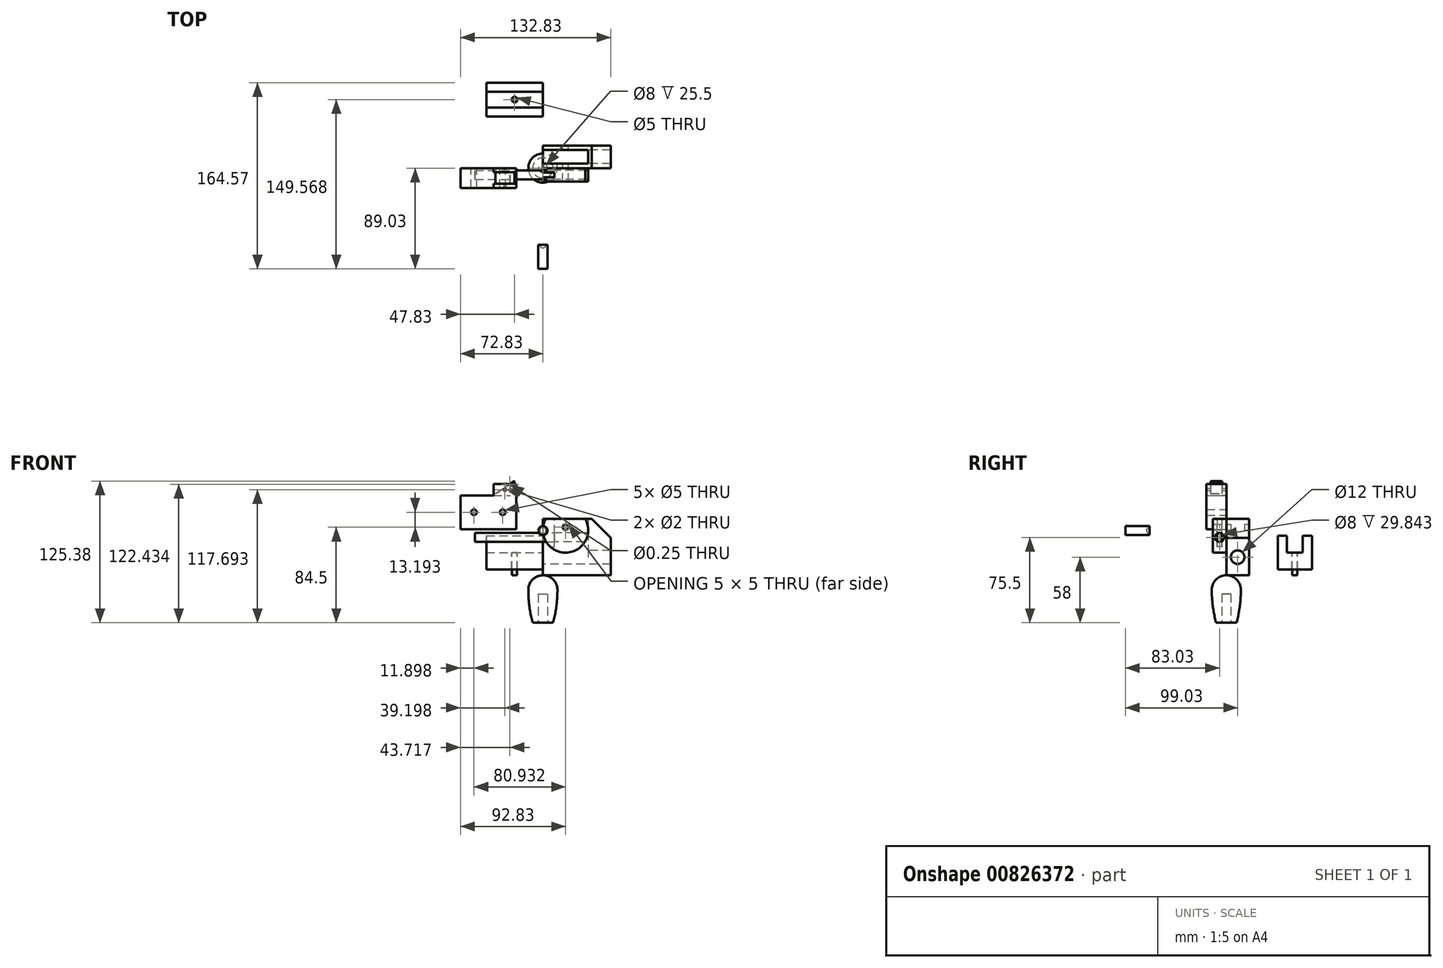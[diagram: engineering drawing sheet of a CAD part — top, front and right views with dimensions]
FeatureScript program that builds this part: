
annotation { "Feature Type Name" : "Feature", "Feature Type Description" : "" }
export const myFeature = defineFeature(function(context is Context, id is Id, definition is map)
    precondition{}
    {
        {
            var Q0;
            Q0=qCreatedBy(makeId("Front.planeOp"),FACE);
            var sketch = newSketch(context, id + "F0", { "sketchPlane" : qUnion([Q0])});
            skLineSegment(sketch, "E0", {"start": v(0, 0) * mm, "end": v(0, 50) * mm});
            skLineSegment(sketch, "E1", {"start": v(0, 50) * mm, "end": v(43, 50) * mm});
            skLineSegment(sketch, "E2", {"start": v(43, 50) * mm, "end": v(60, 33) * mm});
            skLineSegment(sketch, "E3", {"start": v(60, 33) * mm, "end": v(60, 0) * mm});
            skLineSegment(sketch, "E4", {"start": v(60, 0) * mm, "end": v(0, 0) * mm});
            skSolve(sketch);
        }
        {
            var Q0;
            Q0=makeQuery(id+"F0.imprint","IMPRINT",FACE,{"disambiguationData":[TD([[makeQuery(id+"F0.imprint","IMPRINT",EDGE,{"derivedFrom":sQuery(id+"F0.wireOp",EDGE,"E0")}),-1.0]])]});
            extrude(context, id + "F1", {"entities" : qUnion([Q0]), "oppositeDirection" : true, "depth" : 20 * mm, "offsetDistance" : 25 * mm});
        }
        {
            var Q0;
            Q0=makeQuery(id+"F1.opExtrude","SWEPT_FACE",FACE,{"disambiguationData":[OSD([sQuery(id+"F0.wireOp",EDGE,"E0")])]});
            var sketch = newSketch(context, id + "F2", { "sketchPlane" : qUnion([Q0])});
            skLineSegment(sketch, "E5.bottom", {"start": v(-16, 50) * mm, "end": v(-4, 50) * mm});
            skLineSegment(sketch, "E5.top", {"start": v(-16, 16) * mm, "end": v(-4, 16) * mm});
            skLineSegment(sketch, "E5.left", {"start": v(-16, 50) * mm, "end": v(-16, 16) * mm});
            skLineSegment(sketch, "E5.right", {"start": v(-4, 50) * mm, "end": v(-4, 16) * mm});
            skCircle(sketch, "E6", {"center": v(-10, 16) * mm, "radius": 6 * mm});
            skLineSegment(sketch, "E7", {"start": v(-10, 16) * mm, "end": v(-10, 10) * mm});
            skSolve(sketch);
        }
        {
            var Q0;
            Q0 = qSketchRegion(id + "F2", true);
            extrude(context, id + "F3", {"entities" : qUnion([Q0]), "operationType" : NewBodyOperationType.REMOVE, "oppositeDirection" : true, "depth" : 40 * mm, "offsetDistance" : 25 * mm});
        }
        {
            var Q0;
            Q0=makeQuery(id+"F3.boolean.opBoolean","COPY",FACE,{"derivedFrom":makeQuery(id+"F3.opExtrude","CAP_FACE",FACE,{"disambiguationData":[OSD([sQuery(id+"F2.wireOp",EDGE,"E5.bottom"),sQuery(id+"F2.wireOp",EDGE,"E5.left"),sQuery(id+"F2.wireOp",EDGE,"E5.right"),sQuery(id+"F2.wireOp",EDGE,"E6")])],"isStart":false})});
            var sketch = newSketch(context, id + "F4", { "sketchPlane" : qUnion([Q0])});
            skCircle(sketch, "E8", {"center": v(-10, 16) * mm, "radius": 6 * mm});
            skSolve(sketch);
        }
        {
            var Q0;
            {var subQ0=sQuery(id+"F4.wireOp",EDGE,"E8");var subQ1=makeQuery(id+"F4.imprint","INTERSECT",VERTEX,{"derivedFrom":[makeQuery(id+"F3.boolean.opBoolean","COPY",EDGE,{"derivedFrom":makeQuery(id+"F3.opExtrude","CAP_EDGE",EDGE,{"disambiguationData":[OSD([sQuery(id+"F2.wireOp",EDGE,"E5.left")])],"isStart":false})}),subQ0]});Q0=makeQuery(id+"F4.imprint","IMPRINT",FACE,{"disambiguationData":[TD([[makeQuery(id+"F4.imprint","IMPRINT",EDGE,{"disambiguationData":[TD([[subQ1,1.0]])],"derivedFrom":subQ0}),1.0]])]});}
            extrude(context, id + "F5", {"entities" : qUnion([Q0]), "operationType" : NewBodyOperationType.REMOVE, "oppositeDirection" : true, "depth" : 25 * mm, "offsetDistance" : 25 * mm});
        }
        {
            var Q0;
            Q0=qCreatedBy(makeId("Front.planeOp"),FACE);
            var sketch = newSketch(context, id + "F6", { "sketchPlane" : qUnion([Q0])});
            skArc(sketch, "E9", {"start": v(2.68, 50) * mm, "mid": v(20, 20) * mm, "end": v(37.32, 50) * mm});
            skPoint(sketch, "E10", {"position": v(20, 20) * mm});
            skLineSegment(sketch, "E11", {"start": v(2.68, 50) * mm, "end": v(37.32, 50) * mm});
            skSolve(sketch);
        }
        {
            var Q0;
            Q0 = qSketchRegion(id + "F6", true);
            extrude(context, id + "F7", {"entities" : qUnion([Q0]), "depth" : 12 * mm, "offsetDistance" : 25 * mm});
        }
        {
            var Q0;
            Q0=makeQuery(id+"F7.opExtrude","CAP_FACE",FACE,{"disambiguationData":[OSD([sQuery(id+"F6.wireOp",EDGE,"5I9pLb7D-rMst-xJQX-DsKg-gwi81APxeWcW"),sQuery(id+"F6.wireOp",EDGE,"E9")])],"isStart":false});
            var sketch = newSketch(context, id + "F8", { "sketchPlane" : qUnion([Q0])});
            skPoint(sketch, "E12", {"position": v(20, 42.5) * mm});
            skPoint(sketch, "E13", {"position": v(20, 50) * mm});
            skSolve(sketch);
        }
        {
            var Q0;
            Q0=sQuery(id+"F8.wireOp",VERTEX,"E12");
            var Q1;
            Q1=makeQuery(id+"F1.opExtrude","SWEPT_BODY",BODY,{"disambiguationData":[OSD([sQuery(id+"F0.wireOp",EDGE,"E0"),sQuery(id+"F0.wireOp",EDGE,"E1"),sQuery(id+"F0.wireOp",EDGE,"E2"),sQuery(id+"F0.wireOp",EDGE,"E3"),sQuery(id+"F0.wireOp",EDGE,"E4")])]});
            var Q2;
            Q2=makeQuery(id+"F7.opExtrude","SWEPT_BODY",BODY,{"disambiguationData":[OSD([sQuery(id+"F6.wireOp",EDGE,"5I9pLb7D-rMst-xJQX-DsKg-gwi81APxeWcW"),sQuery(id+"F6.wireOp",EDGE,"E9")])]});
            hole(context, id + "F9", {"style" : HoleStyle.SIMPLE, "endStyle" : HoleEndStyle.BLIND, "holeDiameter" : 5 * mm, "majorDiameter" : 5 * mm, "holeDepth" : 50 * mm, "isTappedThrough" : true, "tappedDepth" : 12 * mm, "tapClearance" : 3, "locations" : qUnion([Q0]), "scope" : qUnion([Q1, Q2]), "startStyle" : HoleStartStyle.SKETCH});
        }
        {
            var Q0;
            Q0=makeQuery(id+"F7.opExtrude","SWEPT_FACE",FACE,{"disambiguationData":[OSD([sQuery(id+"F6.wireOp",EDGE,"E11")])]});
            var sketch = newSketch(context, id + "F10", { "sketchPlane" : qUnion([Q0])});
            skLineSegment(sketch, "E14.bottom", {"start": v(0, -3.9) * mm, "end": v(10, -3.9) * mm});
            skLineSegment(sketch, "E14.top", {"start": v(0, -8.1) * mm, "end": v(10, -8.1) * mm});
            skLineSegment(sketch, "E14.left", {"start": v(0, -3.9) * mm, "end": v(0, -8.1) * mm});
            skLineSegment(sketch, "E14.right", {"start": v(10, -3.9) * mm, "end": v(10, -8.1) * mm});
            skSolve(sketch);
        }
        {
            var Q0;
            Q0 = qSketchRegion(id + "F10", true);
            extrude(context, id + "F11", {"entities" : qUnion([Q0]), "operationType" : NewBodyOperationType.REMOVE, "oppositeDirection" : true, "depth" : 25 * mm, "offsetDistance" : 25 * mm});
        }
        {
            var Q0;
            Q0=makeQuery(id+"F11.boolean.opBoolean","COPY",FACE,{"derivedFrom":makeQuery(id+"F11.opExtrude","SWEPT_FACE",FACE,{"disambiguationData":[OSD([sQuery(id+"F10.wireOp",EDGE,"E14.right")])]})});
            var sketch = newSketch(context, id + "F12", { "sketchPlane" : qUnion([Q0])});
            skCircle(sketch, "E15", {"center": v(6, 33.5) * mm, "radius": 4 * mm});
            skPoint(sketch, "E15.centerSnap0", {"position": v(6, 50) * mm});
            skSolve(sketch);
        }
        {
            var Q0;
            Q0 = qSketchRegion(id + "F12", true);
            extrude(context, id + "F13", {"entities" : qUnion([Q0]), "operationType" : NewBodyOperationType.REMOVE, "oppositeDirection" : true, "depth" : 30 * mm, "offsetDistance" : 25 * mm});
        }
        {
            var Q0;
            Q0=makeQuery(id+"F13.boolean.opBoolean","SPLIT",FACE,{"disambiguationData":[TD([makeQuery(id+"F7.opExtrude","SWEPT_FACE",FACE,{"disambiguationData":[OSD([sQuery(id+"F6.wireOp",EDGE,"E11")])]})])],"derivedFrom":makeQuery(id+"F11.boolean.opBoolean","COPY",FACE,{"derivedFrom":makeQuery(id+"F11.opExtrude","SWEPT_FACE",FACE,{"disambiguationData":[OSD([sQuery(id+"F10.wireOp",EDGE,"E14.right")])]})})});
            var sketch = newSketch(context, id + "F14", { "sketchPlane" : qUnion([Q0])});
            skCircle(sketch, "E16", {"center": v(6, 33.5) * mm, "radius": 4 * mm});
            skSolve(sketch);
        }
        {
            var Q0;
            Q0 = qSketchRegion(id + "F14", true);
            extrude(context, id + "F15", {"entities" : qUnion([Q0]), "depth" : 70 * mm, "offsetDistance" : 25 * mm});
        }
        {
            var Q0;
            Q0=qCreatedBy(makeId("Front.planeOp"),FACE);
            var sketch = newSketch(context, id + "F16", { "sketchPlane" : qUnion([Q0])});
            skLineSegment(sketch, "E17", {"start": v(0, -16.5) * mm, "end": v(-4, -16.5) * mm});
            skLineSegment(sketch, "E18", {"start": v(-4, -16.5) * mm, "end": v(-4, -42) * mm});
            skLineSegment(sketch, "E19", {"start": v(0, -16.5) * mm, "end": v(0, 0) * mm});
            skArc(sketch, "E20", {"start": v(0, 0) * mm, "mid": v(-9.09, -3.76) * mm, "end": v(-12.85, -12.85) * mm});
            skLineSegment(sketch, "E21", {"start": v(-4, -42) * mm, "end": v(-9, -42) * mm});
            skArc(sketch, "E22", {"start": v(-12.85, -12.85) * mm, "mid": v(-11.88, -27.55) * mm, "end": v(-9, -42) * mm});
            skLineSegment(sketch, "E23", {"start": v(-12.85, -12.85) * mm, "end": v(0, -12.85) * mm});
            skLineSegment(sketch, "E24", {"start": v(-12.85, -12.85) * mm, "end": v(-12.85, -29.15) * mm});
            skSolve(sketch);
        }
        {
            var Q0;
            Q0 = qSketchRegion(id + "F16", true);
            var Q1;
            Q1=sQuery(id+"F16.wireOp",EDGE,"E19");
            revolve(context, id + "F17", {"surfaceOperationType" : NewSurfaceOperationType.NEW, "entities" : qUnion([Q0]), "axis" : qUnion([Q1]), "revolveType" : RevolveType.FULL});
        }
        {
            var Q0;
            Q0=qCreatedBy(makeId("Front.planeOp"),FACE);
            var sketch = newSketch(context, id + "F18", { "sketchPlane" : qUnion([Q0])});
            skLineSegment(sketch, "E25.bottom", {"start": v(-23.63, 70.7) * mm, "end": v(-72.83, 70.7) * mm});
            skLineSegment(sketch, "E25.top", {"start": v(-23.63, 40.7) * mm, "end": v(-72.83, 40.7) * mm});
            skLineSegment(sketch, "E25.left", {"start": v(-23.63, 70.7) * mm, "end": v(-23.63, 40.7) * mm});
            skLineSegment(sketch, "E25.right", {"start": v(-72.83, 70.7) * mm, "end": v(-72.83, 40.7) * mm});
            skCircle(sketch, "E26", {"center": v(-35.53, 55.7) * mm, "radius": 2.5 * mm});
            skCircle(sketch, "E27", {"center": v(-60.93, 55.7) * mm, "radius": 2.5 * mm});
            skLineSegment(sketch, "E28", {"start": v(-35.53, 55.7) * mm, "end": v(-23.63, 55.7) * mm});
            skLineSegment(sketch, "E29", {"start": v(-60.93, 55.7) * mm, "end": v(-72.83, 55.7) * mm});
            skSolve(sketch);
        }
        {
            var Q0;
            Q0 = qSketchRegion(id + "F18", true);
            extrude(context, id + "F19", {"entities" : qUnion([Q0]), "depth" : 17.5 * mm, "offsetDistance" : 25 * mm});
        }
        {
            var Q0;
            Q0=makeQuery(id+"F19.opExtrude","SWEPT_FACE",FACE,{"disambiguationData":[OSD([sQuery(id+"F18.wireOp",EDGE,"E25.bottom")])]});
            var sketch = newSketch(context, id + "F20", { "sketchPlane" : qUnion([Q0])});
            skLineSegment(sketch, "E30", {"start": v(-43.63, 0) * mm, "end": v(-23.63, 0) * mm});
            skLineSegment(sketch, "E31", {"start": v(-23.63, 0) * mm, "end": v(-23.63, -17.5) * mm});
            skLineSegment(sketch, "E32", {"start": v(-23.63, -17.5) * mm, "end": v(-43.63, -17.5) * mm});
            skLineSegment(sketch, "E33", {"start": v(-43.63, -17.5) * mm, "end": v(-43.63, -13.75) * mm});
            skLineSegment(sketch, "E34", {"start": v(-43.63, -13.75) * mm, "end": v(-28.63, -13.75) * mm});
            skLineSegment(sketch, "E35", {"start": v(-28.63, -13.75) * mm, "end": v(-28.63, -3.75) * mm});
            skLineSegment(sketch, "E36", {"start": v(-28.63, -3.75) * mm, "end": v(-43.63, -3.75) * mm});
            skLineSegment(sketch, "E37", {"start": v(-43.63, 0) * mm, "end": v(-43.63, -3.75) * mm});
            skSolve(sketch);
        }
        {
            var Q0;
            Q0 = qSketchRegion(id + "F20", true);
            extrude(context, id + "F21", {"entities" : qUnion([Q0]), "operationType" : NewBodyOperationType.ADD, "depth" : 10 * mm, "offsetDistance" : 25 * mm});
        }
        {
            var Q0;
            Q0=makeQuery(id+"F21.boolean.opBoolean","MERGE",FACE,{"derivedFrom":[makeQuery(id+"F19.opExtrude","CAP_FACE",FACE,{"disambiguationData":[OSD([sQuery(id+"F18.wireOp",EDGE,"E25.bottom"),sQuery(id+"F18.wireOp",EDGE,"E25.top"),sQuery(id+"F18.wireOp",EDGE,"E25.left"),sQuery(id+"F18.wireOp",EDGE,"E25.right"),sQuery(id+"F18.wireOp",EDGE,"E26"),sQuery(id+"F18.wireOp",EDGE,"E27")])],"isStart":false}),makeQuery(id+"F21.opExtrude","SWEPT_FACE",FACE,{"disambiguationData":[OSD([sQuery(id+"F20.wireOp",EDGE,"E32")])]})]});
            var sketch = newSketch(context, id + "F22", { "sketchPlane" : qUnion([Q0])});
            skCircle(sketch, "E38", {"center": v(-33.63, 75.7) * mm, "radius": 1 * mm});
            skPoint(sketch, "E39", {"position": v(-43.63, 75.7) * mm});
            skPoint(sketch, "E40", {"position": v(-33.63, 80.7) * mm});
            skSolve(sketch);
        }
        {
            var Q0;
            Q0 = qSketchRegion(id + "F22", true);
            extrude(context, id + "F23", {"entities" : qUnion([Q0]), "operationType" : NewBodyOperationType.REMOVE, "oppositeDirection" : true, "depth" : 25 * mm, "offsetDistance" : 25 * mm});
        }
        {
            var Q0;
            Q0=makeQuery(id+"F21.opExtrude","SWEPT_FACE",FACE,{"disambiguationData":[OSD([sQuery(id+"F20.wireOp",EDGE,"E36")])]});
            var sketch = newSketch(context, id + "F24", { "sketchPlane" : qUnion([Q0])});
            skLineSegment(sketch, "E41", {"start": v(-41.8, 72.42) * mm, "end": v(-25.07, 83.38) * mm});
            skLineSegment(sketch, "E42", {"start": v(-25.07, 83.38) * mm, "end": v(-24.8, 82.97) * mm});
            skLineSegment(sketch, "E43", {"start": v(-24.8, 82.97) * mm, "end": v(-41.44, 72.05) * mm});
            skLineSegment(sketch, "E44", {"start": v(-41.44, 72.05) * mm, "end": v(-41.8, 72.42) * mm});
            skCircle(sketch, "E45", {"center": v(-29.11, 80.43) * mm, "radius": 0.12 * mm});
            skPoint(sketch, "E46", {"position": v(-24.93, 83.18) * mm});
            skLineSegment(sketch, "E47", {"start": v(-29.11, 80.43) * mm, "end": v(-24.93, 83.18) * mm});
            skSolve(sketch);
        }
        {
            var Q0;
            Q0 = qSketchRegion(id + "F24", true);
            extrude(context, id + "F25", {"entities" : qUnion([Q0]), "depth" : 10 * mm, "offsetDistance" : 25 * mm});
        }
        {
            var Q0;
            Q0=qCreatedBy(makeId("Right.planeOp"),FACE);
            var sketch = newSketch(context, id + "F26", { "sketchPlane" : qUnion([Q0])});
            skCircle(sketch, "E48", {"center": v(-67.73, 39.46) * mm, "radius": 2.77 * mm});
            skLineSegment(sketch, "E49", {"start": v(-67.73, 39.46) * mm, "end": v(-89.03, 39.46) * mm});
            skLineSegment(sketch, "E50", {"start": v(-89.03, 39.46) * mm, "end": v(-89.03, 43.46) * mm});
            skLineSegment(sketch, "E51", {"start": v(-89.03, 43.46) * mm, "end": v(-67.73, 43.46) * mm});
            skLineSegment(sketch, "E52", {"start": v(-67.73, 43.46) * mm, "end": v(-67.73, 39.46) * mm});
            skSolve(sketch);
        }
        {
            var Q0;
            {var subQ0=sQuery(id+"F26.wireOp",EDGE,"E50");Q0=makeQuery(id+"F26.imprint","IMPRINT",FACE,{"disambiguationData":[TD([[makeQuery(id+"F26.imprint","IMPRINT",EDGE,{"derivedFrom":subQ0}),-1.0]])]});}
            var Q1;
            Q1=sQuery(id+"F26.wireOp",EDGE,"E49");
            revolve(context, id + "F27", {"surfaceOperationType" : NewSurfaceOperationType.NEW, "entities" : qUnion([Q0]), "axis" : qUnion([Q1]), "revolveType" : RevolveType.FULL});
        }
        {
            var Q0;
            {var subQ0=sQuery(id+"F26.wireOp",EDGE,"E49");var subQ1=sQuery(id+"F26.wireOp",EDGE,"E48");var subQ2=makeQuery(id+"F26.imprint","INTERSECT",VERTEX,{"derivedFrom":[subQ1,subQ0]});Q0=makeQuery(id+"F26.imprint","IMPRINT",FACE,{"disambiguationData":[TD([[makeQuery(id+"F26.imprint","IMPRINT",EDGE,{"disambiguationData":[TD([[subQ2,-1.0]])],"derivedFrom":subQ1}),1.0]])]});}
            var sketch = newSketch(context, id + "F28", { "sketchPlane" : qUnion([Q0])});
            skCircle(sketch, "E53", {"center": v(-67.73, 39.46) * mm, "radius": 0.88 * mm});
            skSolve(sketch);
        }
        {
            var Q0;
            Q0 = qSketchRegion(id + "F28", true);
            extrude(context, id + "F29", {"entities" : qUnion([Q0]), "operationType" : NewBodyOperationType.REMOVE, "oppositeDirection" : true, "depth" : 7 * mm, "offsetDistance" : 25 * mm, "symmetric" : true});
        }
        {
            var Q0;
            Q0=qCreatedBy(makeId("Right.planeOp"),FACE);
            var sketch = newSketch(context, id + "F30", { "sketchPlane" : qUnion([Q0])});
            skLineSegment(sketch, "E54", {"start": v(45.54, 5.06) * mm, "end": v(45.54, 35.06) * mm});
            skLineSegment(sketch, "E55", {"start": v(45.54, 35.06) * mm, "end": v(53.54, 35.06) * mm});
            skLineSegment(sketch, "E56", {"start": v(53.54, 35.06) * mm, "end": v(53.54, 20.06) * mm});
            skLineSegment(sketch, "E57", {"start": v(53.54, 20.06) * mm, "end": v(67.54, 20.06) * mm});
            skLineSegment(sketch, "E58", {"start": v(67.54, 20.06) * mm, "end": v(67.54, 35.06) * mm});
            skLineSegment(sketch, "E59", {"start": v(67.54, 35.06) * mm, "end": v(75.54, 35.06) * mm});
            skLineSegment(sketch, "E60", {"start": v(75.54, 35.06) * mm, "end": v(75.54, 5.06) * mm});
            skLineSegment(sketch, "E61", {"start": v(75.54, 5.06) * mm, "end": v(45.54, 5.06) * mm});
            skSolve(sketch);
        }
        {
            var Q0;
            Q0 = qSketchRegion(id + "F30", true);
            extrude(context, id + "F31", {"entities" : qUnion([Q0]), "oppositeDirection" : true, "depth" : 50 * mm, "offsetDistance" : 25 * mm});
        }
        {
            var Q0;
            Q0=makeQuery(id+"F31.opExtrude","SWEPT_FACE",FACE,{"disambiguationData":[OSD([sQuery(id+"F30.wireOp",EDGE,"E57")])]});
            var sketch = newSketch(context, id + "F32", { "sketchPlane" : qUnion([Q0])});
            skCircle(sketch, "E62", {"center": v(-25, 60.54) * mm, "radius": 2.5 * mm});
            skPoint(sketch, "E63", {"position": v(-25, 67.54) * mm});
            skPoint(sketch, "E64", {"position": v(0, 60.54) * mm});
            skSolve(sketch);
        }
        {
            var Q0;
            Q0 = qSketchRegion(id + "F32", true);
            extrude(context, id + "F33", {"entities" : qUnion([Q0]), "operationType" : NewBodyOperationType.REMOVE, "oppositeDirection" : true, "depth" : 25 * mm, "offsetDistance" : 25 * mm});
        }
        {
            var Q0;
            Q0=makeQuery(id+"F31.opExtrude","SWEPT_FACE",FACE,{"disambiguationData":[OSD([sQuery(id+"F30.wireOp",EDGE,"E57")])]});
            var sketch = newSketch(context, id + "F34", { "sketchPlane" : qUnion([Q0])});
            skCircle(sketch, "E65", {"center": v(-25, 60.54) * mm, "radius": 2.25 * mm});
            skSolve(sketch);
        }
        {
            var Q0;
            Q0 = qSketchRegion(id + "F34", true);
            extrude(context, id + "F35", {"entities" : qUnion([Q0]), "oppositeDirection" : true, "depth" : 20 * mm, "offsetDistance" : 25 * mm});
        }
    });
